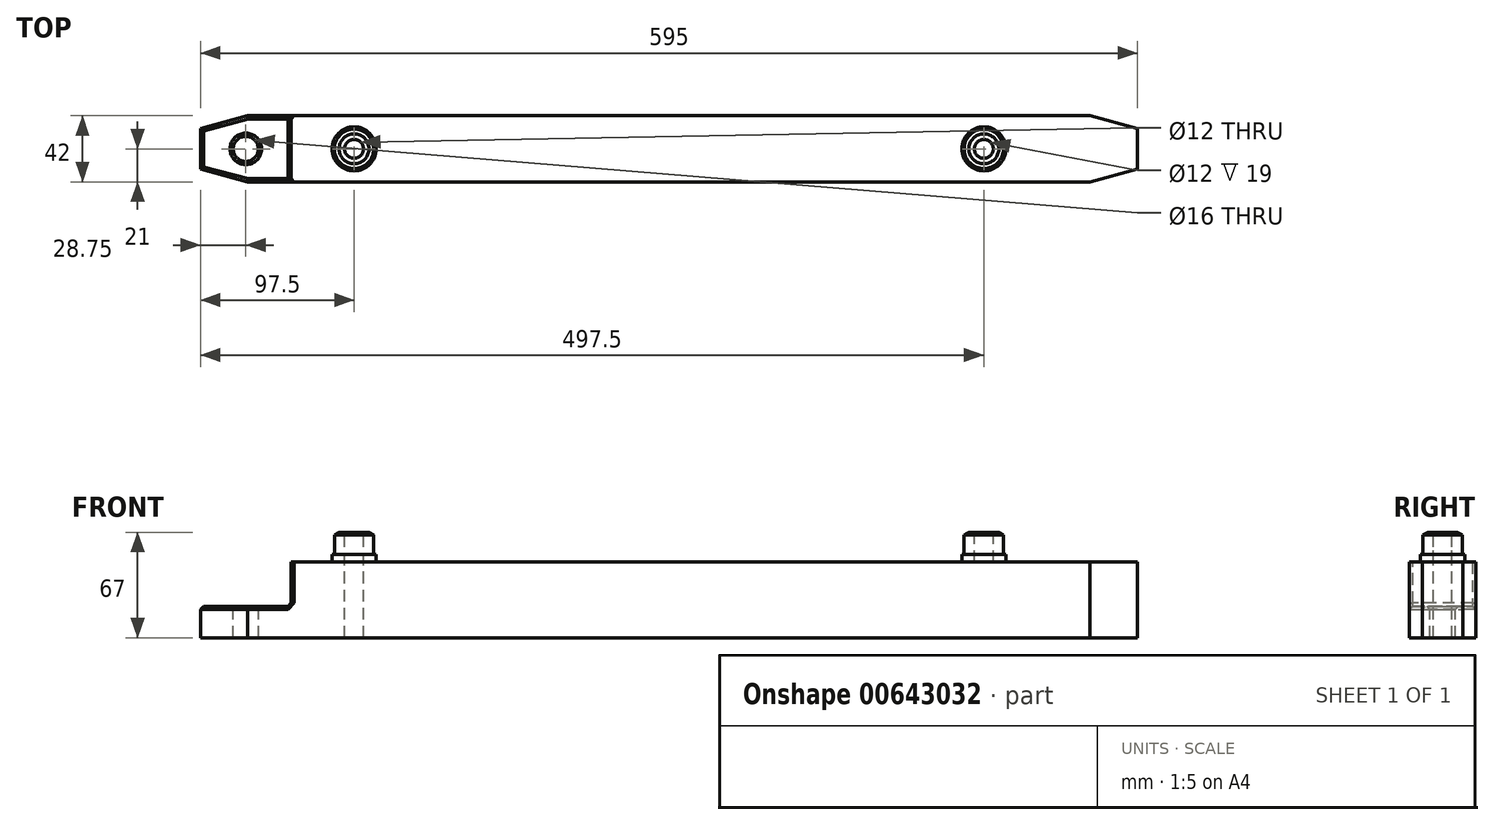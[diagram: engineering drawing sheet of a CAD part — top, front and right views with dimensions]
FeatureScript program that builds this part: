
annotation { "Feature Type Name" : "Feature", "Feature Type Description" : "" }
export const myFeature = defineFeature(function(context is Context, id is Id, definition is map)
    precondition{}
    {
        {
            var Q0;
            Q0=qCreatedBy(makeId("Top.planeOp"),FACE);
            var sketch = newSketch(context, id + "F0", { "sketchPlane" : qUnion([Q0])});
            skLineSegment(sketch, "E0.bottom", {"start": v(297.5, 21) * mm, "end": v(-297.5, 21) * mm});
            skLineSegment(sketch, "E0.top", {"start": v(297.5, -21) * mm, "end": v(-297.5, -21) * mm});
            skLineSegment(sketch, "E0.left", {"start": v(297.5, 21) * mm, "end": v(297.5, -21) * mm});
            skLineSegment(sketch, "E0.right", {"start": v(-297.5, 21) * mm, "end": v(-297.5, -21) * mm});
            skPoint(sketch, "E0.middle", {"position": v(0, 0) * mm});
            skSolve(sketch);
        }
        {
            var Q0;
            Q0=makeQuery(id+"F0.imprint","IMPRINT",FACE,{"disambiguationData":[TD([[makeQuery(id+"F0.imprint","IMPRINT",EDGE,{"derivedFrom":sQuery(id+"F0.wireOp",EDGE,"E0.bottom")}),1.0]])]});
            extrude(context, id + "F1", {"entities" : qUnion([Q0]), "depth" : 48 * mm, "offsetDistance" : 25 * mm});
        }
        {
            var Q0;
            Q0=makeQuery(id+"F1.opExtrude","CAP_FACE",FACE,{"disambiguationData":[OSD([sQuery(id+"F0.wireOp",EDGE,"E0.bottom"),sQuery(id+"F0.wireOp",EDGE,"E0.top"),sQuery(id+"F0.wireOp",EDGE,"E0.left"),sQuery(id+"F0.wireOp",EDGE,"E0.right")])],"isStart":false});
            var sketch = newSketch(context, id + "F2", { "sketchPlane" : qUnion([Q0])});
            skCircle(sketch, "E1", {"center": v(-200, 0) * mm, "radius": 14 * mm});
            skSolve(sketch);
        }
        {
            var Q0;
            Q0=makeQuery(id+"F2.imprint","IMPRINT",FACE,{"disambiguationData":[TD([[makeQuery(id+"F2.imprint","IMPRINT",EDGE,{"derivedFrom":sQuery(id+"F2.wireOp",EDGE,"E1")}),1.0]])]});
            extrude(context, id + "F3", {"entities" : qUnion([Q0]), "depth" : 5 * mm, "offsetDistance" : 25 * mm});
        }
        {
            var Q0;
            Q0=makeQuery(id+"F3.opExtrude","CAP_FACE",FACE,{"disambiguationData":[OSD([sQuery(id+"F2.wireOp",EDGE,"E1")])],"isStart":false});
            var sketch = newSketch(context, id + "F4", { "sketchPlane" : qUnion([Q0])});
            skCircle(sketch, "E2", {"center": v(-200, 0) * mm, "radius": 12.5 * mm});
            skSolve(sketch);
        }
        {
            var Q0;
            Q0=makeQuery(id+"F4.imprint","IMPRINT",FACE,{"disambiguationData":[TD([[makeQuery(id+"F4.imprint","IMPRINT",EDGE,{"derivedFrom":sQuery(id+"F4.wireOp",EDGE,"E2")}),1.0]])]});
            extrude(context, id + "F5", {"entities" : qUnion([Q0]), "operationType" : NewBodyOperationType.ADD, "depth" : (19 - 5) * mm, "offsetDistance" : 25 * mm});
        }
        {
            var Q0;
            Q0=makeQuery(id+"F5.opExtrude","CAP_EDGE",EDGE,{"disambiguationData":[OSD([sQuery(id+"F4.wireOp",EDGE,"E2")])],"isStart":false});
            chamfer(context, id + "F6", {"entities" : qUnion([Q0]), "chamferType" : ChamferType.OFFSET_ANGLE, "width" : 3 * mm, "oppositeDirection" : false, "angle" : 30 * degree, "tangentPropagation" : true});
        }
        {
            var Q0;
            Q0=makeQuery(id+"F5.opExtrude","CAP_FACE",FACE,{"disambiguationData":[OSD([sQuery(id+"F4.wireOp",EDGE,"E2")])],"isStart":false});
            var sketch = newSketch(context, id + "F7", { "sketchPlane" : qUnion([Q0])});
            skCircle(sketch, "E3", {"center": v(-200, 0) * mm, "radius": 6 * mm});
            skSolve(sketch);
        }
        {
            var Q0;
            Q0=makeQuery(id+"F7.imprint","IMPRINT",FACE,{"disambiguationData":[TD([[makeQuery(id+"F7.imprint","IMPRINT",EDGE,{"derivedFrom":sQuery(id+"F7.wireOp",EDGE,"E3")}),1.0]])]});
            extrude(context, id + "F8", {"entities" : qUnion([Q0]), "operationType" : NewBodyOperationType.REMOVE, "endBound" : BoundingType.THROUGH_ALL, "oppositeDirection" : true, "depth" : 25 * mm, "offsetDistance" : 25 * mm});
        }
        {
            var Q0;
            Q0=makeQuery(id+"F3.opExtrude","SWEPT_BODY",BODY,{"disambiguationData":[OSD([sQuery(id+"F2.wireOp",EDGE,"E1")])]});
            var Q1;
            Q1=qCreatedBy(makeId("Right.planeOp"),FACE);
            mirror(context, id + "F9", {"operationType" : NewBodyOperationType.ADD, "entities" : qUnion([Q0]), "mirrorPlane" : qUnion([Q1])});
        }
        {
            var Q0;
            {var subQ0=sQuery(id+"F0.wireOp",EDGE,"E0.left");var subQ1=sQuery(id+"F0.wireOp",EDGE,"E0.top");var subQ2=sQuery(id+"F0.wireOp",EDGE,"E0.right");var subQ3=sQuery(id+"F0.wireOp",EDGE,"E0.bottom");Q0=makeQuery(id+"F9.boolean.opBoolean","SPLIT",FACE,{"disambiguationData":[TD([makeQuery(id+"F1.opExtrude","SWEPT_FACE",FACE,{"disambiguationData":[OSD([subQ3])]})])],"derivedFrom":makeQuery(id+"F1.opExtrude","CAP_FACE",FACE,{"disambiguationData":[OSD([subQ3,subQ1,subQ0,subQ2])],"isStart":false})});}
            var sketch = newSketch(context, id + "F10", { "sketchPlane" : qUnion([Q0])});
            skLineSegment(sketch, "E4.bottom", {"start": v(-297.5, 21) * mm, "end": v(-240, 21) * mm});
            skLineSegment(sketch, "E4.top", {"start": v(-297.5, -21) * mm, "end": v(-240, -21) * mm});
            skLineSegment(sketch, "E4.left", {"start": v(-297.5, 21) * mm, "end": v(-297.5, -21) * mm});
            skLineSegment(sketch, "E4.right", {"start": v(-240, 21) * mm, "end": v(-240, -21) * mm});
            skSolve(sketch);
        }
        {
            var Q0;
            Q0=makeQuery(id+"F10.imprint","IMPRINT",FACE,{"disambiguationData":[TD([[makeQuery(id+"F10.imprint","IMPRINT",EDGE,{"derivedFrom":sQuery(id+"F10.wireOp",EDGE,"E4.bottom")}),1.0]])]});
            extrude(context, id + "F11", {"entities" : qUnion([Q0]), "operationType" : NewBodyOperationType.REMOVE, "oppositeDirection" : true, "depth" : 28 * mm, "offsetDistance" : 25 * mm});
        }
        {
            var Q0;
            Q0=makeQuery(id+"F11.boolean.opBoolean","COPY",FACE,{"derivedFrom":makeQuery(id+"F11.opExtrude","CAP_FACE",FACE,{"disambiguationData":[OSD([sQuery(id+"F10.wireOp",EDGE,"E4.bottom"),sQuery(id+"F10.wireOp",EDGE,"E4.top"),sQuery(id+"F10.wireOp",EDGE,"E4.left"),sQuery(id+"F10.wireOp",EDGE,"E4.right")])],"isStart":false})});
            var sketch = newSketch(context, id + "F12", { "sketchPlane" : qUnion([Q0])});
            skCircle(sketch, "E5", {"center": v(-268.75, 0) * mm, "radius": 8 * mm});
            skPoint(sketch, "E5.centerSnap0", {"position": v(-268.75, 21) * mm});
            skSolve(sketch);
        }
        {
            var Q0;
            Q0=makeQuery(id+"F12.imprint","IMPRINT",FACE,{"disambiguationData":[TD([[makeQuery(id+"F12.imprint","IMPRINT",EDGE,{"derivedFrom":sQuery(id+"F12.wireOp",EDGE,"E5")}),1.0]])]});
            extrude(context, id + "F13", {"entities" : qUnion([Q0]), "operationType" : NewBodyOperationType.REMOVE, "endBound" : BoundingType.THROUGH_ALL, "oppositeDirection" : true, "depth" : 25 * mm, "offsetDistance" : 25 * mm});
        }
        {
            var Q0;
            Q0=makeQuery(id+"F1.opExtrude","SWEPT_EDGE",EDGE,{"disambiguationData":[OSD([sQuery(id+"F0.wireOp",EDGE,"E0.top"),sQuery(id+"F0.wireOp",EDGE,"E0.right")])]});
            var Q1;
            Q1=makeQuery(id+"F1.opExtrude","SWEPT_EDGE",EDGE,{"disambiguationData":[OSD([sQuery(id+"F0.wireOp",EDGE,"E0.bottom"),sQuery(id+"F0.wireOp",EDGE,"E0.right")])]});
            var Q2;
            Q2=makeQuery(id+"F1.opExtrude","SWEPT_EDGE",EDGE,{"disambiguationData":[OSD([sQuery(id+"F0.wireOp",EDGE,"E0.top"),sQuery(id+"F0.wireOp",EDGE,"E0.left")])]});
            var Q3;
            Q3=makeQuery(id+"F1.opExtrude","SWEPT_EDGE",EDGE,{"disambiguationData":[OSD([sQuery(id+"F0.wireOp",EDGE,"E0.bottom"),sQuery(id+"F0.wireOp",EDGE,"E0.left")])]});
            chamfer(context, id + "F14", {"entities" : qUnion([Q0, Q1, Q2, Q3]), "chamferType" : ChamferType.OFFSET_ANGLE, "width" : 30 * mm, "oppositeDirection" : false, "angle" : 15 * degree, "tangentPropagation" : true});
        }
        {
            var Q0;
            Q0=makeQuery(id+"F11.boolean.opBoolean","COPY",FACE,{"derivedFrom":makeQuery(id+"F11.opExtrude","CAP_FACE",FACE,{"disambiguationData":[OSD([sQuery(id+"F10.wireOp",EDGE,"E4.bottom"),sQuery(id+"F10.wireOp",EDGE,"E4.top"),sQuery(id+"F10.wireOp",EDGE,"E4.left"),sQuery(id+"F10.wireOp",EDGE,"E4.right")])],"isStart":false})});
            var Q1;
            Q1=makeQuery(id+"Fkah163lSGyZMdu_1.1.F11.boolean.opBoolean","COPY",FACE,{"derivedFrom":makeQuery(id+"Fkah163lSGyZMdu_1.1.F11.opExtrude","CAP_FACE",FACE,{"disambiguationData":[OSD([sQuery(id+"F10.wireOp",EDGE,"E4.bottom"),sQuery(id+"F10.wireOp",EDGE,"E4.top"),sQuery(id+"F10.wireOp",EDGE,"E4.left"),sQuery(id+"F10.wireOp",EDGE,"E4.right")])],"isStart":false})});
            chamfer(context, id + "F15", {"entities" : qUnion([Q0, Q1]), "width" : 2 * mm, "tangentPropagation" : true});
        }
    });
